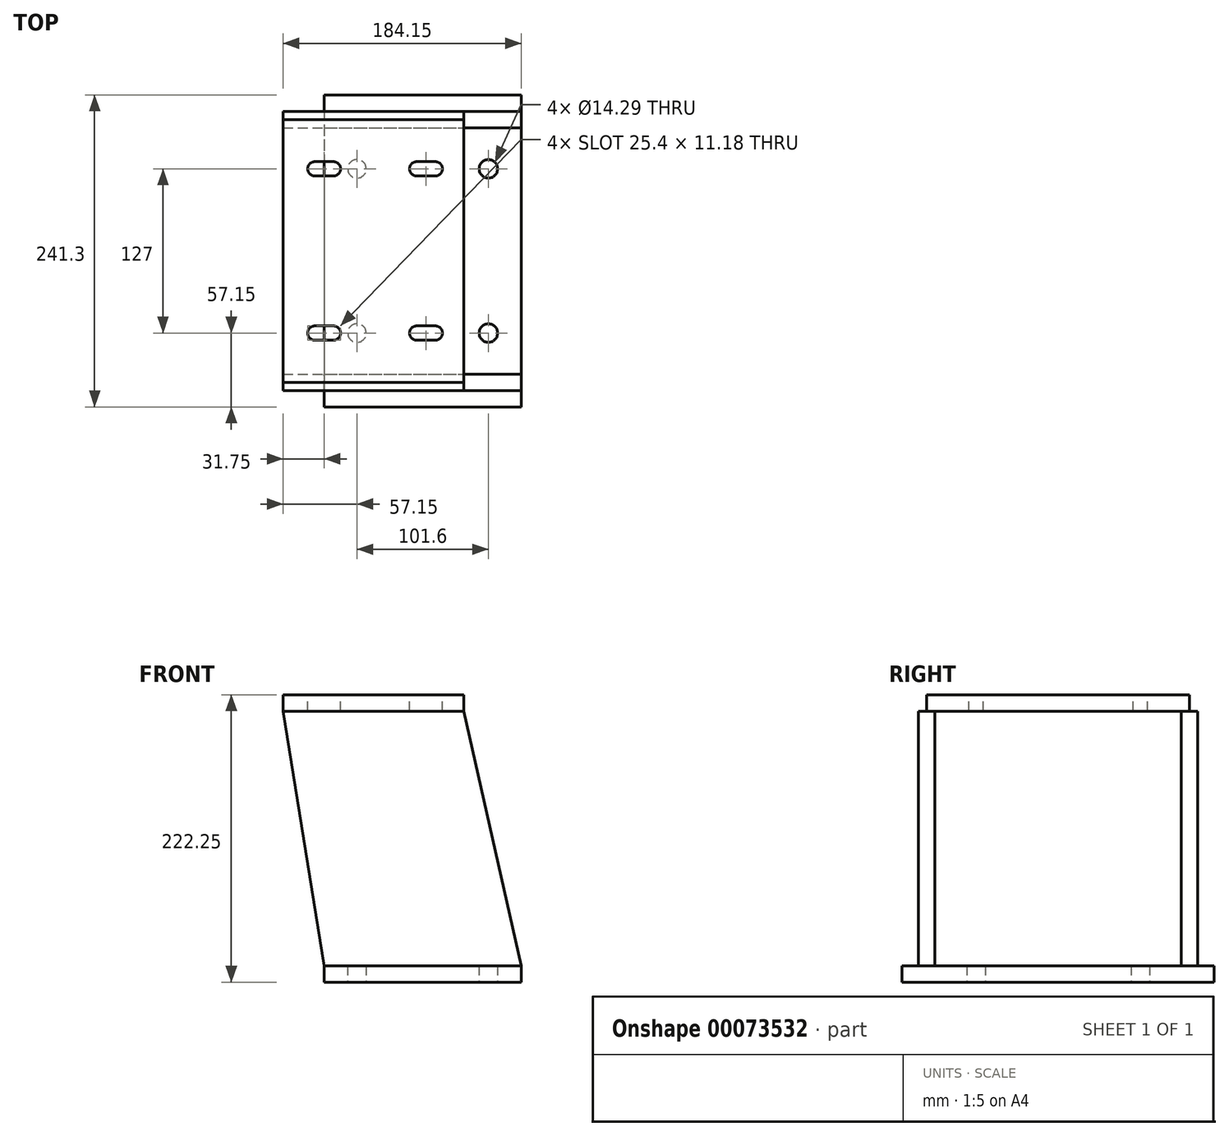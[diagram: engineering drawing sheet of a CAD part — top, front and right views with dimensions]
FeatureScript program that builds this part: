
annotation { "Feature Type Name" : "Feature", "Feature Type Description" : "" }
export const myFeature = defineFeature(function(context is Context, id is Id, definition is map)
    precondition{}
    {
        {
            var Q0;
            Q0=qCreatedBy(makeId("Top.planeOp"),FACE);
            var sketch = newSketch(context, id + "F0", { "sketchPlane" : qUnion([Q0])});
            skLineSegment(sketch, "E0.rect.bottom", {"start": v(-76.2, 120.65) * mm, "end": v(76.2, 120.65) * mm});
            skLineSegment(sketch, "E0.rect.top", {"start": v(-76.2, -120.65) * mm, "end": v(76.2, -120.65) * mm});
            skLineSegment(sketch, "E0.rect.left", {"start": v(-76.2, 120.65) * mm, "end": v(-76.2, -120.65) * mm});
            skLineSegment(sketch, "E0.rect.right", {"start": v(76.2, 120.65) * mm, "end": v(76.2, -120.65) * mm});
            skPoint(sketch, "E0.rect.middle", {"position": v(0, 0) * mm});
            skLineSegment(sketch, "E1", {"start": v(0, -142.72) * mm, "end": v(0, 120.65) * mm, "construction": true});
            skPoint(sketch, "E1.startSnap0", {"position": v(0, 120.65) * mm});
            skLineSegment(sketch, "E2", {"start": v(-76.2, 0) * mm, "end": v(76.2, 0) * mm, "construction": true});
            skLineSegment(sketch, "E3.0", {"start": v(-50.8, -142.72) * mm, "end": v(-50.8, 120.65) * mm, "construction": true});
            skLineSegment(sketch, "E4.0", {"start": v(-76.2, 63.5) * mm, "end": v(76.2, 63.5) * mm, "construction": true});
            skCircle(sketch, "E5", {"center": v(-50.8, 63.5) * mm, "radius": 7.14 * mm});
            skCircle(sketch, "E6.MirrorC", {"center": v(50.8, 63.5) * mm, "radius": 7.14 * mm});
            skCircle(sketch, "E7.MirrorC", {"center": v(-50.8, -63.5) * mm, "radius": 7.14 * mm});
            skCircle(sketch, "E8.MirrorC", {"center": v(50.8, -63.5) * mm, "radius": 7.14 * mm});
            skSolve(sketch);
        }
        {
            var Q0;
            Q0 = qSketchRegion(id + "F0", true);
            extrude(context, id + "F1", {"entities" : qUnion([Q0]), "depth" : 12.7 * mm});
        }
        {
            var Q0;
            Q0=qCreatedBy(makeId("Top.planeOp"),FACE);
            cPlane(context, id + "F2", {"entities" : qUnion([Q0]), "cplaneType" : CPlaneType.OFFSET, "offset" : 222.25 * mm, "width" : 152.4 * mm, "height" : 152.4 * mm});
        }
        {
            var Q0;
            Q0=qCreatedBy(id+"F2.planeOp",FACE);
            var sketch = newSketch(context, id + "F3", { "sketchPlane" : qUnion([Q0])});
            skLineSegment(sketch, "E9.0", {"start": v(76.2, 120.65) * mm, "end": v(76.2, -120.65) * mm, "construction": true});
            skLineSegment(sketch, "E10.0", {"start": v(-107.95, 120.65) * mm, "end": v(-107.95, -120.65) * mm, "construction": true});
            skLineSegment(sketch, "E11", {"start": v(-232.66, 0) * mm, "end": v(161.6, 0) * mm, "construction": true});
            skLineSegment(sketch, "E12.0", {"start": v(-232.66, 101.6) * mm, "end": v(161.6, 101.6) * mm, "construction": true});
            skLineSegment(sketch, "E13.bottom", {"start": v(-107.95, 101.6) * mm, "end": v(31.75, 101.6) * mm});
            skLineSegment(sketch, "E13.top", {"start": v(-107.95, -101.6) * mm, "end": v(31.75, -101.6) * mm});
            skLineSegment(sketch, "E13.left", {"start": v(-107.95, 101.6) * mm, "end": v(-107.95, -101.6) * mm});
            skLineSegment(sketch, "E13.right", {"start": v(31.75, 101.6) * mm, "end": v(31.75, -101.6) * mm});
            skLineSegment(sketch, "E14", {"start": v(-35.53, 101.6) * mm, "end": v(-35.53, -101.6) * mm, "construction": true});
            skLineSegment(sketch, "E15.0", {"start": v(-232.66, 63.5) * mm, "end": v(161.6, 63.5) * mm, "construction": true});
            skLineSegment(sketch, "E16.0", {"start": v(2.57, 101.6) * mm, "end": v(2.57, -101.6) * mm, "construction": true});
            skLineSegment(sketch, "E17.0", {"start": v(-76.2, 120.65) * mm, "end": v(-76.2, -120.65) * mm, "construction": true});
            skLineSegment(sketch, "E18.0", {"start": v(-83.31, 120.65) * mm, "end": v(-83.31, -120.65) * mm, "construction": true});
            skLineSegment(sketch, "E19.0", {"start": v(-69.09, 120.65) * mm, "end": v(-69.09, -120.65) * mm, "construction": true});
            skLineSegment(sketch, "E20.0", {"start": v(9.68, 101.6) * mm, "end": v(9.68, -101.6) * mm, "construction": true});
            skLineSegment(sketch, "E21.0", {"start": v(-4.55, 101.6) * mm, "end": v(-4.55, -101.6) * mm, "construction": true});
            skLineSegment(sketch, "E22", {"start": v(-83.31, 63.5) * mm, "end": v(-69.09, 63.5) * mm});
            skLineSegment(sketch, "E23", {"start": v(-4.55, 63.5) * mm, "end": v(9.68, 63.5) * mm});
            skArc(sketch, "E24.0.startCap", {"start": v(-83.31, 57.91) * mm, "mid": v(-88.9, 63.5) * mm, "end": v(-83.31, 69.09) * mm});
            skArc(sketch, "E24.0.endCap", {"start": v(-69.09, 69.09) * mm, "mid": v(-63.5, 63.5) * mm, "end": v(-69.09, 57.91) * mm});
            skLineSegment(sketch, "E24.0.left", {"start": v(-83.31, 69.09) * mm, "end": v(-69.09, 69.09) * mm});
            skLineSegment(sketch, "E24.0.right", {"start": v(-83.31, 57.91) * mm, "end": v(-69.09, 57.91) * mm});
            skArc(sketch, "E24.1.startCap", {"start": v(-4.55, 57.91) * mm, "mid": v(-10.13, 63.5) * mm, "end": v(-4.55, 69.09) * mm});
            skArc(sketch, "E24.1.endCap", {"start": v(9.68, 69.09) * mm, "mid": v(15.27, 63.5) * mm, "end": v(9.68, 57.91) * mm});
            skLineSegment(sketch, "E24.1.left", {"start": v(-4.55, 69.09) * mm, "end": v(9.68, 69.09) * mm});
            skLineSegment(sketch, "E24.1.right", {"start": v(-4.55, 57.91) * mm, "end": v(9.68, 57.91) * mm});
            skLineSegment(sketch, "E25.MirrorCS", {"start": v(-83.31, -63.5) * mm, "end": v(-69.09, -63.5) * mm});
            skArc(sketch, "E26.MirrorCS", {"start": v(-83.31, -57.91) * mm, "mid": v(-88.9, -63.5) * mm, "end": v(-83.31, -69.09) * mm});
            skLineSegment(sketch, "E27.MirrorCS", {"start": v(-83.31, -69.09) * mm, "end": v(-69.09, -69.09) * mm});
            skArc(sketch, "E28.MirrorCS", {"start": v(-4.55, -57.91) * mm, "mid": v(-10.13, -63.5) * mm, "end": v(-4.55, -69.09) * mm});
            skArc(sketch, "E29.MirrorCS", {"start": v(9.68, -69.09) * mm, "mid": v(15.27, -63.5) * mm, "end": v(9.68, -57.91) * mm});
            skLineSegment(sketch, "E30.MirrorCS", {"start": v(-4.55, -57.91) * mm, "end": v(9.68, -57.91) * mm});
            skLineSegment(sketch, "E31.MirrorCS", {"start": v(-4.55, -63.5) * mm, "end": v(9.68, -63.5) * mm});
            skArc(sketch, "E32.MirrorCS", {"start": v(-69.09, -69.09) * mm, "mid": v(-63.5, -63.5) * mm, "end": v(-69.09, -57.91) * mm});
            skLineSegment(sketch, "E33.MirrorCS", {"start": v(-4.55, -69.09) * mm, "end": v(9.68, -69.09) * mm});
            skLineSegment(sketch, "E34.MirrorCS", {"start": v(-83.31, -57.91) * mm, "end": v(-69.09, -57.91) * mm});
            skSolve(sketch);
        }
        {
            var Q0;
            Q0 = qSketchRegion(id + "F3", true);
            extrude(context, id + "F4", {"entities" : qUnion([Q0]), "oppositeDirection" : true, "depth" : 12.7 * mm});
        }
        {
            var Q0;
            Q0=qCreatedBy(makeId("Front.planeOp"),FACE);
            cPlane(context, id + "F5", {"entities" : qUnion([Q0]), "cplaneType" : CPlaneType.OFFSET, "offset" : 95.25 * mm, "width" : 152.4 * mm, "height" : 152.4 * mm});
        }
        {
            var Q0;
            Q0=qCreatedBy(id+"F5.planeOp",FACE);
            var sketch = newSketch(context, id + "F6", { "sketchPlane" : qUnion([Q0])});
            skLineSegment(sketch, "E35.0", {"start": v(-107.95, 209.55) * mm, "end": v(31.75, 209.55) * mm});
            skLineSegment(sketch, "E36.0", {"start": v(-76.2, 12.7) * mm, "end": v(76.2, 12.7) * mm});
            skLineSegment(sketch, "E37", {"start": v(31.75, 209.55) * mm, "end": v(76.2, 12.7) * mm});
            skLineSegment(sketch, "E38", {"start": v(-107.95, 209.55) * mm, "end": v(-76.2, 12.7) * mm});
            skSolve(sketch);
        }
        {
            var Q0;
            Q0 = qSketchRegion(id + "F6", true);
            extrude(context, id + "F7", {"entities" : qUnion([Q0]), "depth" : 12.7 * mm});
        }
        {
            var Q0;
            Q0=makeQuery(id+"F7.opExtrude","SWEPT_BODY",BODY,{"disambiguationData":[OSD([sQuery(id+"F6.wireOp",EDGE,"E35.0"),sQuery(id+"F6.wireOp",EDGE,"E36.0"),sQuery(id+"F6.wireOp",EDGE,"E37"),sQuery(id+"F6.wireOp",EDGE,"E38")])]});
            var Q1;
            Q1=qCreatedBy(makeId("Front.planeOp"),FACE);
            mirror(context, id + "F8", {"entities" : qUnion([Q0]), "mirrorPlane" : qUnion([Q1])});
        }
    });
